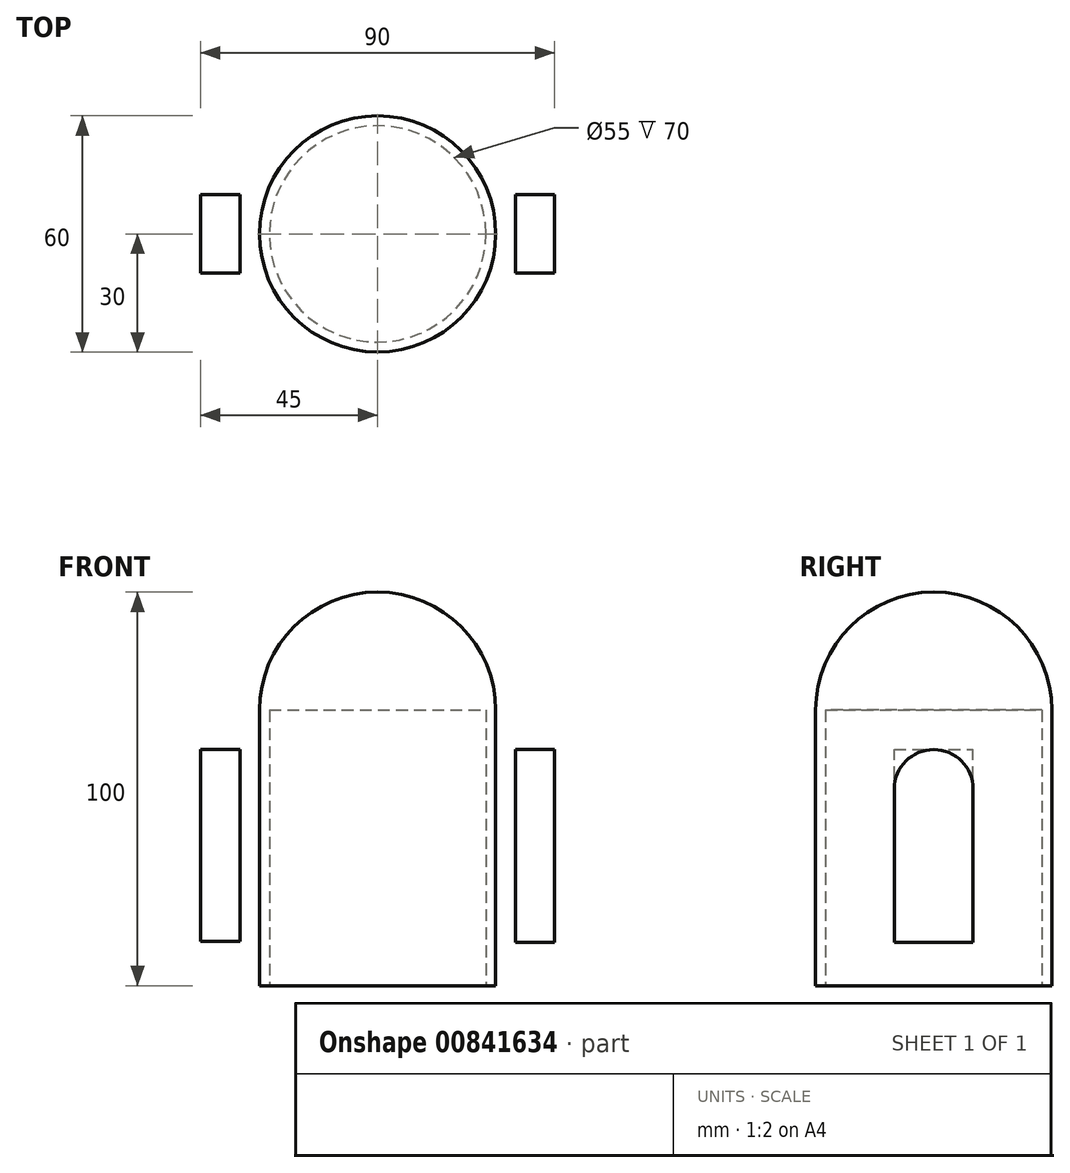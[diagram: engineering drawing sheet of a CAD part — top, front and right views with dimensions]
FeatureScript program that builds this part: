
annotation { "Feature Type Name" : "Feature", "Feature Type Description" : "" }
export const myFeature = defineFeature(function(context is Context, id is Id, definition is map)
    precondition{}
    {
        {
            var Q0;
            Q0=qCreatedBy(makeId("Top.planeOp"),FACE);
            var sketch = newSketch(context, id + "F0", { "sketchPlane" : qUnion([Q0])});
            skCircle(sketch, "E0", {"center": v(0, 0) * mm, "radius": 30 * mm});
            skSolve(sketch);
        }
        {
            var Q0;
            Q0=makeQuery(id+"F0.imprint","IMPRINT",FACE,{"disambiguationData":[TD([[makeQuery(id+"F0.imprint","IMPRINT",EDGE,{"derivedFrom":sQuery(id+"F0.wireOp",EDGE,"E0")}),1.0]])]});
            extrude(context, id + "F1", {"entities" : qUnion([Q0]), "depth" : 70 * mm, "offsetDistance" : 25 * mm});
        }
        {
            var Q0;
            Q0=makeQuery(id+"F1.opExtrude","CAP_FACE",FACE,{"disambiguationData":[OSD([sQuery(id+"F0.wireOp",EDGE,"E0")])],"isStart":false});
            var sketch = newSketch(context, id + "F2", { "sketchPlane" : qUnion([Q0])});
            skLineSegment(sketch, "E1", {"start": v(0, 30) * mm, "end": v(0, -30) * mm});
            skCircle(sketch, "E2", {"center": v(0, 0) * mm, "radius": 30 * mm});
            skSolve(sketch);
        }
        {
            var Q0;
            {var subQ0=sQuery(id+"F2.wireOp",EDGE,"E1");Q0=makeQuery(id+"F2.imprint","IMPRINT",FACE,{"disambiguationData":[TD([[makeQuery(id+"F2.imprint","IMPRINT",EDGE,{"derivedFrom":subQ0}),-1.0]])]});}
            var Q1;
            Q1=sQuery(id+"F2.wireOp",EDGE,"E1");
            revolve(context, id + "F3", {"operationType" : NewBodyOperationType.ADD, "surfaceOperationType" : NewSurfaceOperationType.NEW, "entities" : qUnion([Q0]), "axis" : qUnion([Q1]), "revolveType" : RevolveType.FULL});
        }
        {
            var Q0;
            Q0=qCreatedBy(makeId("Front.planeOp"),FACE);
            var sketch = newSketch(context, id + "F4", { "sketchPlane" : qUnion([Q0])});
            skLineSegment(sketch, "E3", {"start": v(-35, 60) * mm, "end": v(35, 60) * mm});
            skLineSegment(sketch, "E4", {"start": v(35, 60) * mm, "end": v(35, 10.95) * mm});
            skLineSegment(sketch, "E5", {"start": v(35, 10.95) * mm, "end": v(45, 10.95) * mm});
            skLineSegment(sketch, "E6", {"start": v(45, 10.95) * mm, "end": v(45, 60) * mm});
            skLineSegment(sketch, "E7", {"start": v(45, 60) * mm, "end": v(35, 60) * mm});
            skLineSegment(sketch, "E8", {"start": v(-35, 60) * mm, "end": v(-45, 60) * mm});
            skLineSegment(sketch, "E9", {"start": v(-45, 60) * mm, "end": v(-45, 11.3) * mm});
            skLineSegment(sketch, "E10", {"start": v(-45, 11.3) * mm, "end": v(-35, 11.3) * mm});
            skLineSegment(sketch, "E11", {"start": v(-35, 11.3) * mm, "end": v(-35, 60) * mm});
            skSolve(sketch);
        }
        {
            var Q0;
            Q0 = qSketchRegion(id + "F4", true);
            var Q1;
            Q1=makeQuery(id+"F4.imprint","IMPRINT",FACE,{"disambiguationData":[TD([[makeQuery(id+"F4.imprint","IMPRINT",EDGE,{"derivedFrom":sQuery(id+"F4.wireOp",EDGE,"E8")}),1.0]])]});
            extrude(context, id + "F5", {"entities" : qUnion([Q0, Q1]), "endBound" : BoundingType.SYMMETRIC, "depth" : 20 * mm, "offsetDistance" : 25 * mm});
        }
        {
            var Q0;
            Q0=makeQuery(id+"F1.opExtrude","CAP_FACE",FACE,{"disambiguationData":[OSD([sQuery(id+"F0.wireOp",EDGE,"E0")])],"isStart":true});
            var sketch = newSketch(context, id + "F6", { "sketchPlane" : qUnion([Q0])});
            skCircle(sketch, "E12", {"center": v(0, 0) * mm, "radius": 27.5 * mm});
            skSolve(sketch);
        }
        {
            var Q0;
            Q0=makeQuery(id+"F6.imprint","IMPRINT",FACE,{"disambiguationData":[TD([[makeQuery(id+"F6.imprint","IMPRINT",EDGE,{"derivedFrom":sQuery(id+"F6.wireOp",EDGE,"E12")}),1.0]])]});
            extrude(context, id + "F7", {"entities" : qUnion([Q0]), "operationType" : NewBodyOperationType.REMOVE, "oppositeDirection" : true, "depth" : 70 * mm, "offsetDistance" : 25 * mm});
        }
        {
            var Q0;
            Q0=makeQuery(id+"F5.opExtrude","CAP_EDGE",EDGE,{"disambiguationData":[OSD([sQuery(id+"F4.wireOp",EDGE,"E7")])],"isStart":true});
            fillet(context, id + "F8", {"entities" : qUnion([Q0]), "radius" : 10 * mm, "tangentPropagation" : true, "allowEdgeOverflow" : false});
        }
        {
            var Q0;
            Q0=makeQuery(id+"F5.opExtrude","CAP_EDGE",EDGE,{"disambiguationData":[OSD([sQuery(id+"F4.wireOp",EDGE,"E7")])],"isStart":false});
            fillet(context, id + "F9", {"entities" : qUnion([Q0]), "radius" : 10 * mm, "tangentPropagation" : true, "allowEdgeOverflow" : false});
        }
    });
